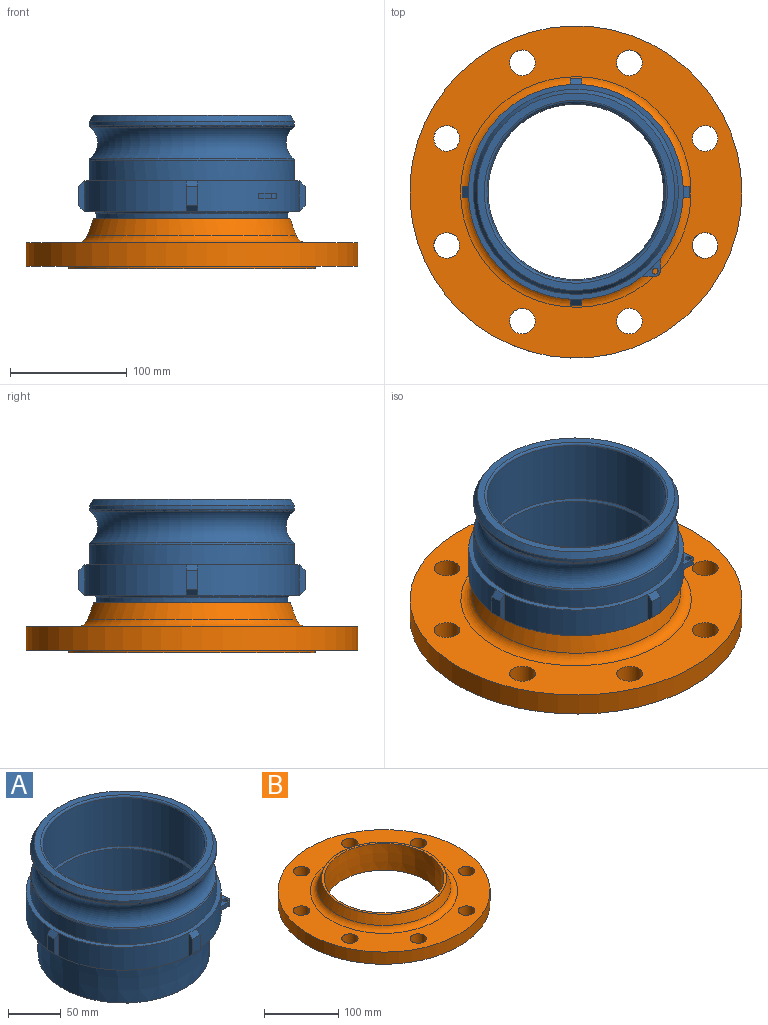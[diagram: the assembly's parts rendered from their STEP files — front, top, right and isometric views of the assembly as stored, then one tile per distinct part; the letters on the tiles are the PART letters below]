
ASSEMBLY  parts=2 mates=1
PART A: 46 faces, bbox 212.5x212.5x128.5 mm
  f0: cylinder r=92.25mm len=87.11mm, axis (0,0,-1), area 3482mm2, adj f12,f14,f21,f27,f36,f38,f39,f40
  f1: cylinder r=92.25mm len=87.11mm, axis (0,0,-1), area 3588.4mm2, adj f12,f14,f26,f32
  f2: cylinder r=92.25mm len=87.11mm, axis (0,0,-1), area 3588.4mm2, adj f12,f14,f16,f22
  f3: plane 161.84x161.84mm, normal (0,0,-1), area 2757.1mm2, adj f4,f15
  f4: cylinder r=75.3mm len=150.6mm, axis (0,0,-1), area 32409mm2, adj f3,f5
  f5: cone r=75.3mm half-angle=30deg, axis (0,0,1), area 1144.5mm2, adj f4,f6
  f6: cylinder r=76.5mm len=153mm, axis (0,0,-1), area 26879.5mm2, adj f5,f42
  f7: plane 169.45x169.45mm, normal (0,0,1), area 3191.9mm2, adj f8,f42
  f8: cone r=84.72mm half-angle=30deg, axis (0,0,-1), area 3444.2mm2, adj f7,f9
  f9: cylinder r=87.9mm len=175.8mm, axis (0,0,-1), area 1667.9mm2, adj f8,f43
  f10: torus R=98.15mm, axis (0,0,-1), area 16017.5mm2, adj f43,f44
  f11: cylinder r=87.9mm len=175.8mm, axis (0,0,-1), area 9620.9mm2, adj f12,f44
  f12: plane 184.5x184.5mm, normal (0,0,1), area 2463.7mm2, adj f0,f1,f2,f11,f13,f16,f17,f19
  f13: cylinder r=92.25mm len=87.11mm, axis (0,0,-1), area 3588.4mm2, adj f12,f14,f17,f31
  f14: plane 184.5x184.5mm, normal (0,0,-1), area 4417.2mm2, adj f0,f1,f2,f13,f16,f17,f18,f21
  f15: cone r=82.35mm half-angle=1.8deg, axis (0,0,1), area 22603mm2, adj f3,f45
  f16: plane 26.6x5.14mm, normal (0,-1,0), area 111.6mm2, adj f2,f12,f14,f18,f19,f20
  f17: plane 26.6x5.14mm, normal (0,1,0), area 111.6mm2, adj f12,f13,f14,f18,f19,f20
  f18: plane 10x5mm, normal (-0.71,0,-0.71), area 70.7mm2, adj f14,f16,f17,f20
  f19: plane 10x5mm, normal (-0.71,0,0.71), area 70.7mm2, adj f12,f16,f17,f20
  f20: plane 16.6x10mm, normal (-1,0,0), area 166mm2, adj f16,f17,f18,f19
  f21: plane 26.6x5.14mm, normal (1,0,0), area 111.6mm2, adj f0,f12,f14,f23,f24,f25
  f22: plane 26.6x5.14mm, normal (-1,0,0), area 111.6mm2, adj f2,f12,f14,f23,f24,f25
  f23: plane 10x5mm, normal (0,-0.71,-0.71), area 70.7mm2, adj f14,f21,f22,f25
  f24: plane 10x5mm, normal (0,-0.71,0.71), area 70.7mm2, adj f12,f21,f22,f25
  f25: plane 16.6x10mm, normal (0,-1,0), area 166mm2, adj f21,f22,f23,f24
  f26: plane 26.6x5.14mm, normal (0,1,0), area 111.6mm2, adj f1,f12,f14,f28,f29,f30
  f27: plane 26.6x5.14mm, normal (0,-1,0), area 111.6mm2, adj f0,f12,f14,f28,f29,f30
  f28: plane 10x5mm, normal (0.71,0,-0.71), area 70.7mm2, adj f14,f26,f27,f30
  f29: plane 10x5mm, normal (0.71,0,0.71), area 70.7mm2, adj f12,f26,f27,f30
  f30: plane 16.6x10mm, normal (1,0,0), area 166mm2, adj f26,f27,f28,f29
  f31: plane 26.6x5.14mm, normal (-1,0,0), area 111.6mm2, adj f12,f13,f14,f33,f34,f35
  f32: plane 26.6x5.14mm, normal (1,0,0), area 111.6mm2, adj f1,f12,f14,f33,f34,f35
  f33: plane 10x5mm, normal (0,0.71,-0.71), area 70.7mm2, adj f14,f31,f32,f35
  f34: plane 10x5mm, normal (0,0.71,0.71), area 70.7mm2, adj f12,f31,f32,f35
  f35: plane 16.6x10mm, normal (0,1,0), area 166mm2, adj f31,f32,f33,f34
  f36: plane 11.01x5mm, normal (1,0,0), area 55mm2, adj f0,f39,f40,f41
  f37: cylinder r=2.5mm len=5mm, axis (0,0,-1), area 78.5mm2, adj f39,f40
  f38: plane 11.01x5mm, normal (0,-1,0), area 55mm2, adj f0,f39,f40,f41
  f39: plane 15.01x15.01mm, normal (0,0,1), area 80.9mm2, adj f0,f36,f37,f38,f41
  f40: plane 15.01x15.01mm, normal (0,0,-1), area 80.9mm2, adj f0,f36,f37,f38,f41
  f41: cylinder r=4mm len=5mm, axis (0,0,-1), area 31.4mm2, adj f36,f38,f39,f40
  f42: torus R=78.5mm, axis (0,0,-1), area 1524.4mm2, adj f6,f7
  f43: torus R=85.9mm, axis (0,0,1), area 975mm2, adj f9,f10
  f44: torus R=85.9mm, axis (0,0,1), area 975mm2, adj f10,f11
  f45: torus R=84.29mm, axis (0,0,1), area 1606.5mm2, adj f14,f15
PART B: 18 faces, bbox 285x285x43 mm
  f0: plane 168.3x168.3mm, normal (0,0,1), area 1855.1mm2, adj f1,f8
  f1: cone r=80.56mm half-angle=1.8deg, axis (0,0,1), area 21596.4mm2, adj f0,f2
  f2: plane 212x212mm, normal (0,0,-1), area 15579.8mm2, adj f1,f3
  f3: cylinder r=106mm len=212mm, axis (0,0,1), area 1332mm2, adj f2,f4
  f4: plane 285x285mm, normal (0,0,-1), area 25454mm2, adj f3,f5,f9,f10,f11,f12,f13,f14
  f5: cylinder r=142.5mm len=285mm, axis (0,0,1), area 17907.1mm2, adj f4,f6
  f6: plane 285x285mm, normal (0,0,1), area 30000.9mm2, adj f5,f9,f10,f11,f12,f13,f14,f15
  f7: cone r=92mm half-angle=20.5deg, axis (0,0,-1), area 8448.7mm2, adj f8,f17
  f8: cylinder r=84.15mm len=168.3mm, axis (0,0,1), area 0.5mm2, adj f0,f7
  f9: cylinder r=11mm len=22mm, axis (0,0,1), area 1382.3mm2, adj f4,f6
  f10: cylinder r=11mm len=22mm, axis (0,0,1), area 1382.3mm2, adj f4,f6
  f11: cylinder r=11mm len=22mm, axis (0,0,1), area 1382.3mm2, adj f4,f6
  f12: cylinder r=11mm len=22mm, axis (0,0,1), area 1382.3mm2, adj f4,f6
  f13: cylinder r=11mm len=22mm, axis (0,0,1), area 1382.3mm2, adj f4,f6
  f14: cylinder r=11mm len=22mm, axis (0,0,1), area 1382.3mm2, adj f4,f6
  f15: cylinder r=11mm len=22mm, axis (0,0,1), area 1382.3mm2, adj f4,f6
  f16: cylinder r=11mm len=22mm, axis (0,0,1), area 1382.3mm2, adj f4,f6
  f17: torus R=98.94mm, axis (0,0,-1), area 7132.6mm2, adj f6,f7
PLACE A t=(-1.09,-1.14,-19.26)mm
PLACE B t=(-1.09,-1.14,-22.26)mm fixed
MATE fastened A.f0 <-> B.f1  axis (0,0,1) through (-1.09,-1.14,-19.26)mm
